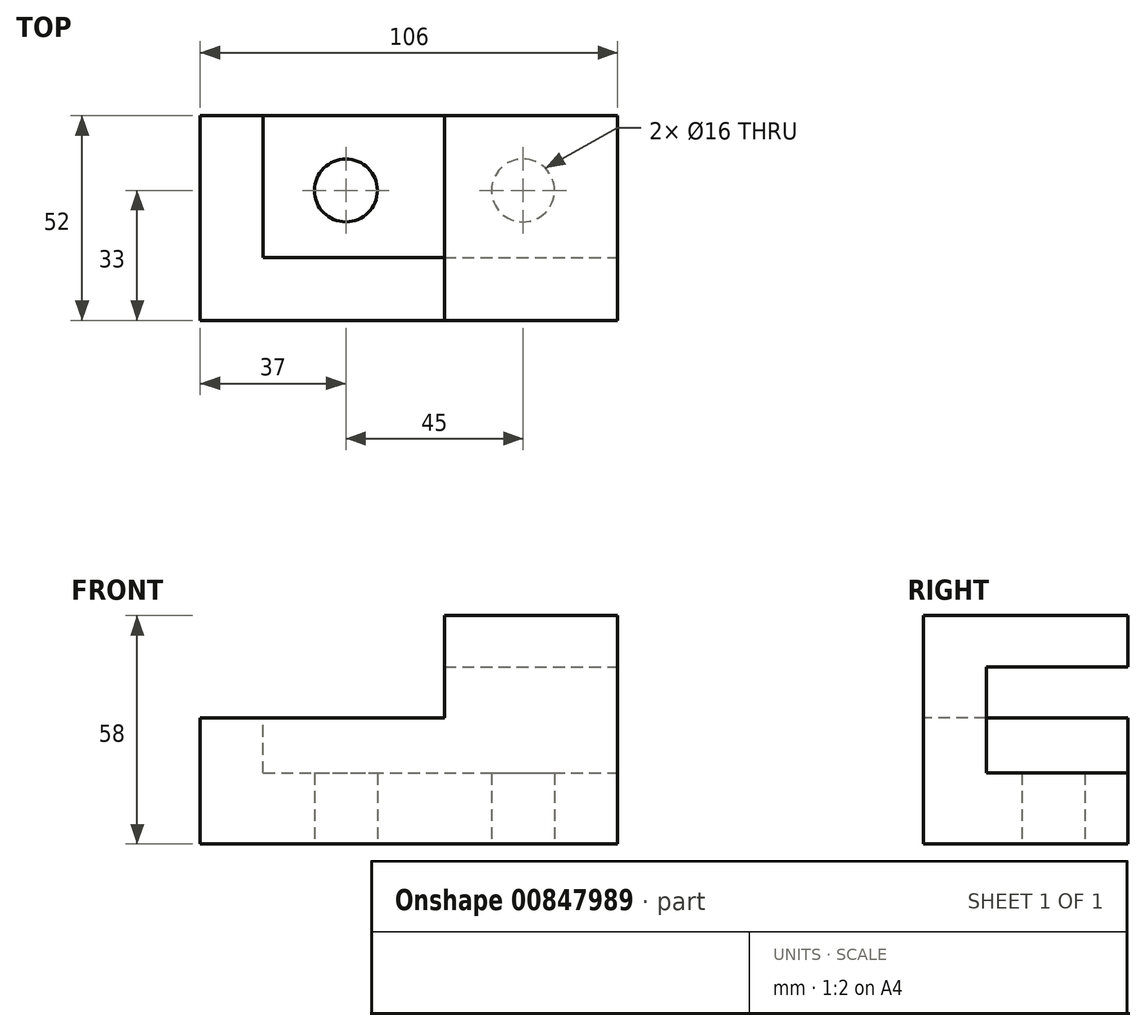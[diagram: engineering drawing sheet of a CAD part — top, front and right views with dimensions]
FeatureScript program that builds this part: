
annotation { "Feature Type Name" : "Feature", "Feature Type Description" : "" }
export const myFeature = defineFeature(function(context is Context, id is Id, definition is map)
    precondition{}
    {
        {
            var Q0;
            Q0=qCreatedBy(makeId("Front.planeOp"),FACE);
            var sketch = newSketch(context, id + "F0", { "sketchPlane" : qUnion([Q0])});
            skLineSegment(sketch, "E0.bottom", {"start": v(0, 0) * mm, "end": v(106, 0) * mm});
            skLineSegment(sketch, "E0.top", {"start": v(0, 58) * mm, "end": v(106, 58) * mm});
            skLineSegment(sketch, "E0.left", {"start": v(0, 0) * mm, "end": v(0, 58) * mm});
            skLineSegment(sketch, "E0.right", {"start": v(106, 0) * mm, "end": v(106, 58) * mm});
            skSolve(sketch);
        }
        {
            var Q0;
            Q0=makeQuery(id+"F0.imprint","IMPRINT",FACE,{"disambiguationData":[TD([[makeQuery(id+"F0.imprint","IMPRINT",EDGE,{"derivedFrom":sQuery(id+"F0.wireOp",EDGE,"E0.bottom")}),1.0]])]});
            extrude(context, id + "F1", {"entities" : qUnion([Q0]), "depth" : 52 * mm, "offsetDistance" : 25.4 * mm});
        }
        {
            var Q0;
            Q0=makeQuery(id+"F1.opExtrude","CAP_FACE",FACE,{"disambiguationData":[OSD([sQuery(id+"F0.wireOp",EDGE,"E0.bottom"),sQuery(id+"F0.wireOp",EDGE,"E0.top"),sQuery(id+"F0.wireOp",EDGE,"E0.left"),sQuery(id+"F0.wireOp",EDGE,"E0.right")])],"isStart":false});
            var sketch = newSketch(context, id + "F2", { "sketchPlane" : qUnion([Q0])});
            skLineSegment(sketch, "E1", {"start": v(0, 0) * mm, "end": v(0, 32) * mm});
            skLineSegment(sketch, "E2", {"start": v(0, 32) * mm, "end": v(62, 32) * mm});
            skLineSegment(sketch, "E3", {"start": v(62, 32) * mm, "end": v(62, 58) * mm});
            skLineSegment(sketch, "E4", {"start": v(62, 58) * mm, "end": v(106, 58) * mm});
            skSolve(sketch);
        }
        {
            var Q0;
            {var subQ0=sQuery(id+"F2.wireOp",EDGE,"E2");Q0=makeQuery(id+"F2.imprint","IMPRINT",FACE,{"disambiguationData":[TD([[makeQuery(id+"F2.imprint","IMPRINT",EDGE,{"derivedFrom":subQ0}),1.0]])]});}
            extrude(context, id + "F3", {"entities" : qUnion([Q0]), "operationType" : NewBodyOperationType.REMOVE, "endBound" : BoundingType.THROUGH_ALL, "oppositeDirection" : true, "depth" : 25.4 * mm, "offsetDistance" : 25.4 * mm});
        }
        {
            var Q0;
            Q0=makeQuery(id+"F1.opExtrude","SWEPT_FACE",FACE,{"disambiguationData":[OSD([sQuery(id+"F0.wireOp",EDGE,"E0.right")])]});
            var sketch = newSketch(context, id + "F4", { "sketchPlane" : qUnion([Q0])});
            skLineSegment(sketch, "E5", {"start": v(0, 0) * mm, "end": v(0, 18) * mm});
            skLineSegment(sketch, "E6", {"start": v(0, 18) * mm, "end": v(-36, 18) * mm});
            skLineSegment(sketch, "E7", {"start": v(-36, 18) * mm, "end": v(-36, 45) * mm});
            skLineSegment(sketch, "E8", {"start": v(-36, 45) * mm, "end": v(0, 45) * mm});
            skLineSegment(sketch, "E9", {"start": v(0, 45) * mm, "end": v(0, 58) * mm});
            skSolve(sketch);
        }
        {
            var Q0;
            {var subQ0=sQuery(id+"F4.wireOp",EDGE,"E6");Q0=makeQuery(id+"F4.imprint","IMPRINT",FACE,{"disambiguationData":[TD([[makeQuery(id+"F4.imprint","IMPRINT",EDGE,{"derivedFrom":subQ0}),-1.0]])]});}
            extrude(context, id + "F5", {"entities" : qUnion([Q0]), "operationType" : NewBodyOperationType.REMOVE, "oppositeDirection" : true, "depth" : 90 * mm, "offsetDistance" : 25.4 * mm});
        }
        {
            var Q0;
            Q0=makeQuery(id+"F1.opExtrude","SWEPT_FACE",FACE,{"disambiguationData":[OSD([sQuery(id+"F0.wireOp",EDGE,"E0.bottom")])]});
            var sketch = newSketch(context, id + "F6", { "sketchPlane" : qUnion([Q0])});
            skLineSegment(sketch, "E10", {"start": v(106, 52) * mm, "end": v(106, 19) * mm});
            skLineSegment(sketch, "E11", {"start": v(106, 19) * mm, "end": v(82, 19) * mm});
            skLineSegment(sketch, "E12", {"start": v(82, 19) * mm, "end": v(82, 52) * mm});
            skLineSegment(sketch, "E13", {"start": v(82, 52) * mm, "end": v(37, 52) * mm});
            skLineSegment(sketch, "E14", {"start": v(37, 52) * mm, "end": v(37, 19) * mm});
            skCircle(sketch, "E15", {"center": v(37, 19) * mm, "radius": 8 * mm});
            skCircle(sketch, "E16", {"center": v(82, 19) * mm, "radius": 8 * mm});
            skSolve(sketch);
        }
        {
            var Q0;
            Q0 = qSketchRegion(id + "F6", true);
            extrude(context, id + "F7", {"entities" : qUnion([Q0]), "operationType" : NewBodyOperationType.REMOVE, "oppositeDirection" : true, "depth" : 18 * mm, "offsetDistance" : 25.4 * mm});
        }
    });
